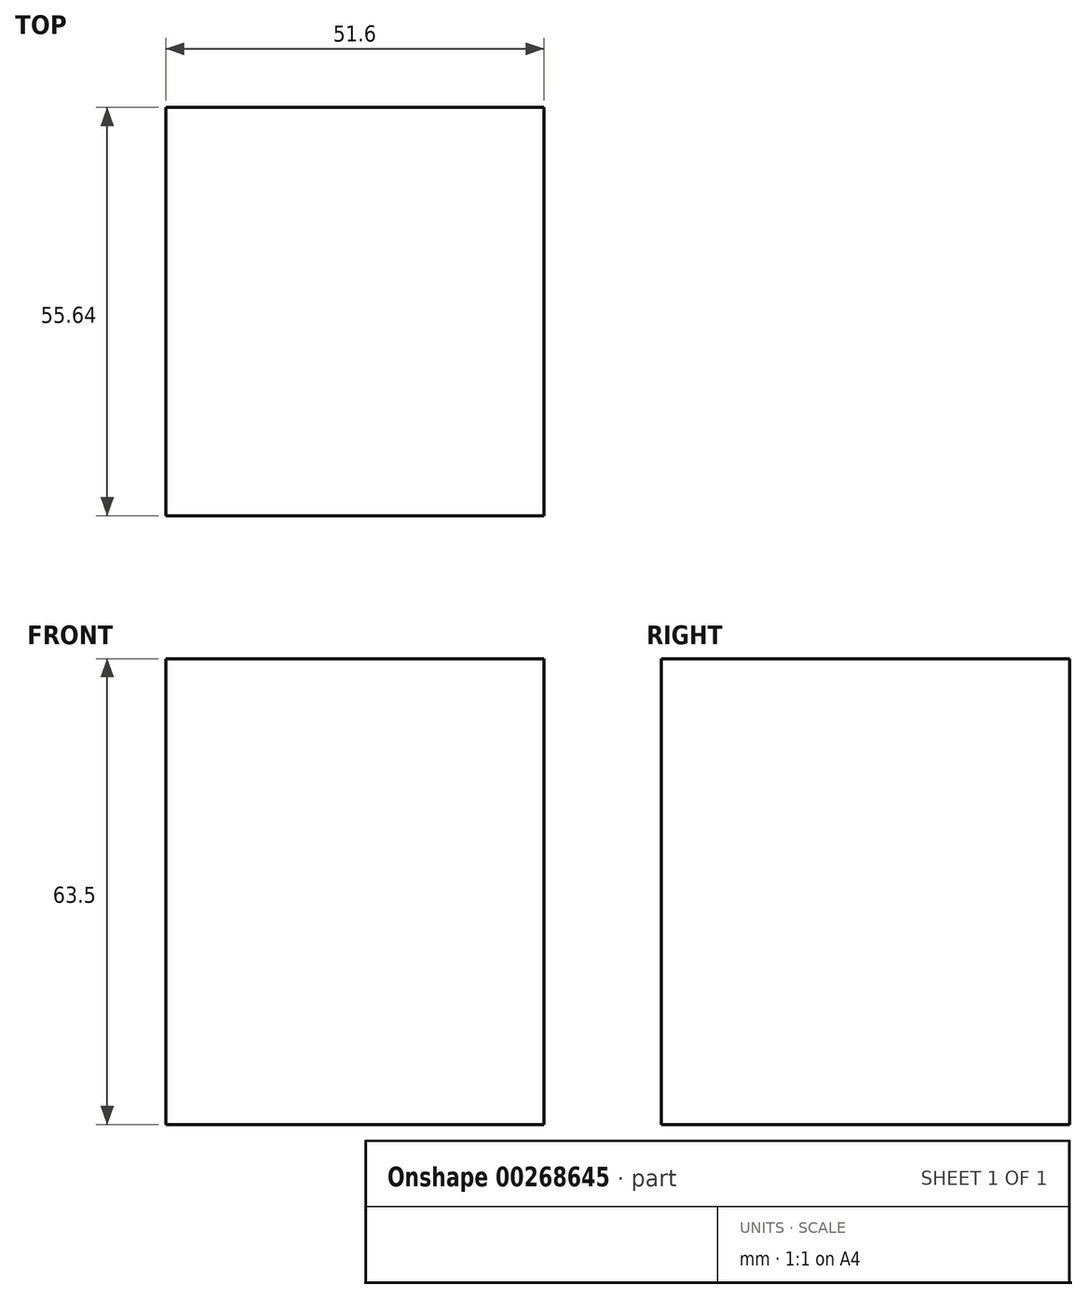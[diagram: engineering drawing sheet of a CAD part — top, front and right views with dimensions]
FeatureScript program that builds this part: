
annotation { "Feature Type Name" : "Feature", "Feature Type Description" : "" }
export const myFeature = defineFeature(function(context is Context, id is Id, definition is map)
    precondition{}
    {
        {
            var Q0;
            Q0=qCreatedBy(makeId("Top.planeOp"),FACE);
            var sketch = newSketch(context, id + "F0", { "sketchPlane" : qUnion([Q0])});
            skLineSegment(sketch, "E0.bottom", {"start": v(-25.8, 27.82) * mm, "end": v(25.8, 27.82) * mm});
            skLineSegment(sketch, "E0.top", {"start": v(-25.8, -27.82) * mm, "end": v(25.8, -27.82) * mm});
            skLineSegment(sketch, "E0.left", {"start": v(-25.8, 27.82) * mm, "end": v(-25.8, -27.82) * mm});
            skLineSegment(sketch, "E0.right", {"start": v(25.8, 27.82) * mm, "end": v(25.8, -27.82) * mm});
            skPoint(sketch, "E0.middle", {"position": v(0, 0) * mm});
            skSolve(sketch);
        }
        {
            var Q0;
            Q0=makeQuery(id+"F0.imprint","IMPRINT",FACE,{"disambiguationData":[TD([[makeQuery(id+"F0.imprint","IMPRINT",EDGE,{"derivedFrom":sQuery(id+"F0.wireOp",EDGE,"E0.bottom")}),-1.0]])]});
            extrude(context, id + "F1", {"entities" : qUnion([Q0]), "depth" : 63.5 * mm, "offsetDistance" : 25.4 * mm});
        }
    });
